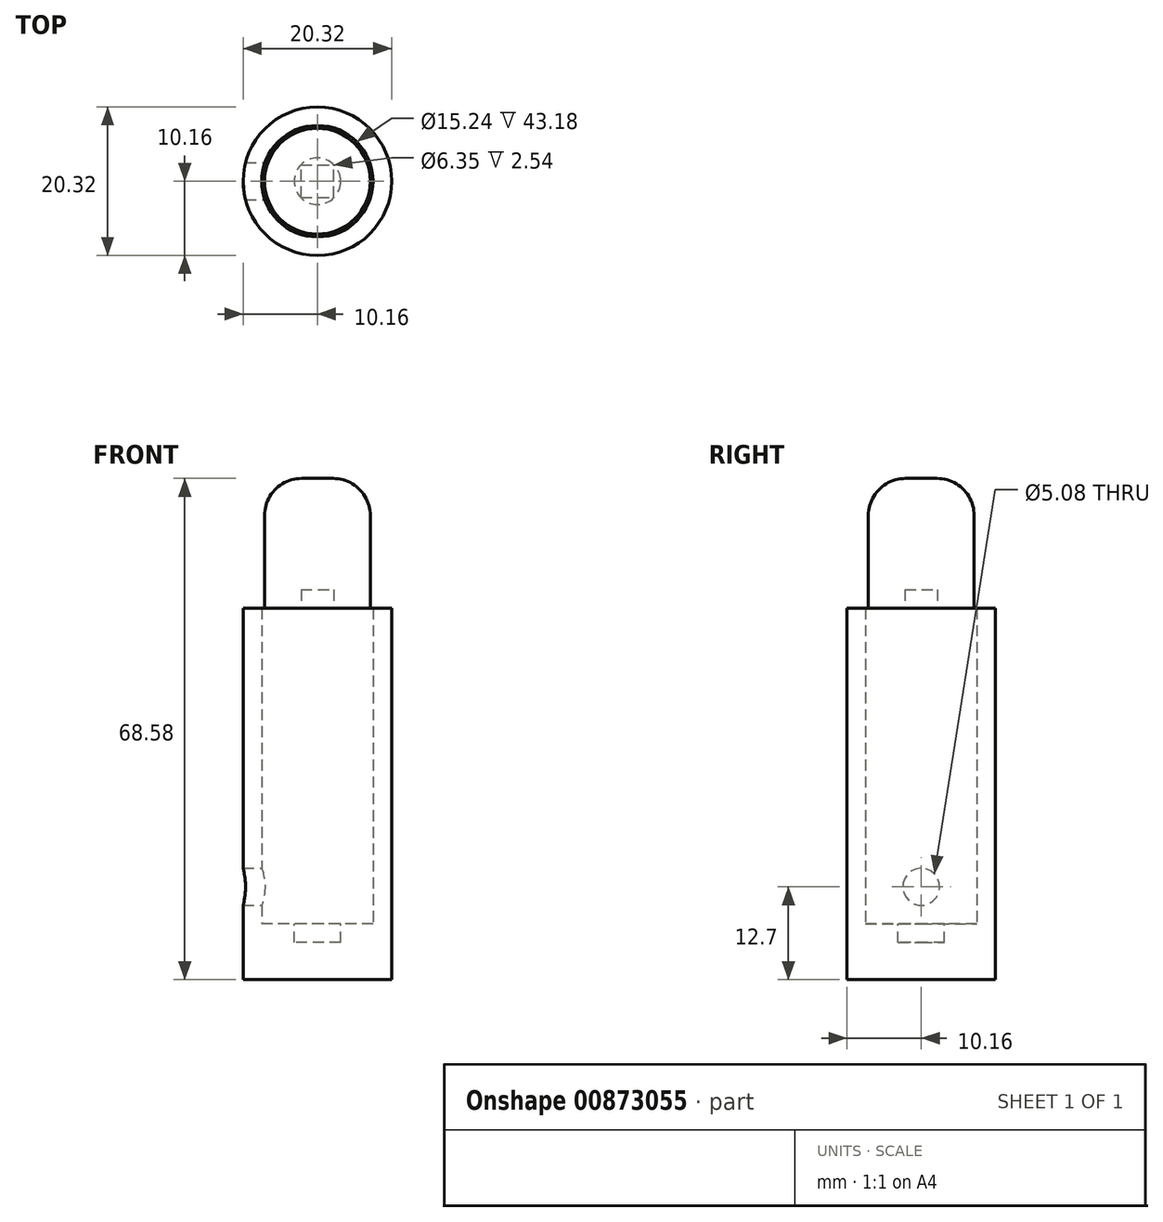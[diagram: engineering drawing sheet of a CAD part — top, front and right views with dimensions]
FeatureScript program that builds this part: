
annotation { "Feature Type Name" : "Feature", "Feature Type Description" : "" }
export const myFeature = defineFeature(function(context is Context, id is Id, definition is map)
    precondition{}
    {
        {
            var Q0;
            Q0=qCreatedBy(makeId("Top.planeOp"),FACE);
            var sketch = newSketch(context, id + "F0", { "sketchPlane" : qUnion([Q0])});
            skCircle(sketch, "E0", {"center": v(0, 0) * mm, "radius": 10.16 * mm});
            skSolve(sketch);
        }
        {
            var Q0;
            Q0=makeQuery(id+"F0.imprint","IMPRINT",FACE,{"disambiguationData":[TD([[makeQuery(id+"F0.imprint","IMPRINT",EDGE,{"derivedFrom":sQuery(id+"F0.wireOp",EDGE,"E0")}),1.0]])]});
            extrude(context, id + "F1", {"entities" : qUnion([Q0]), "depth" : 7.62 * mm, "offsetDistance" : 25.4 * mm});
        }
        {
            var Q0;
            Q0=makeQuery(id+"F1.opExtrude","CAP_FACE",FACE,{"disambiguationData":[OSD([sQuery(id+"F0.wireOp",EDGE,"E0")])],"isStart":false});
            var sketch = newSketch(context, id + "F2", { "sketchPlane" : qUnion([Q0])});
            skCircle(sketch, "E1", {"center": v(0, 0) * mm, "radius": 3.43 * mm});
            skCircle(sketch, "E2", {"center": v(0, 0) * mm, "radius": 7.62 * mm});
            skSolve(sketch);
        }
        {
            var Q0;
            Q0=makeQuery(id+"F2.imprint","IMPRINT",FACE,{"disambiguationData":[TD([[makeQuery(id+"F2.imprint","IMPRINT",EDGE,{"derivedFrom":sQuery(id+"F2.wireOp",EDGE,"E2")}),-1.0]])]});
            extrude(context, id + "F3", {"entities" : qUnion([Q0]), "operationType" : NewBodyOperationType.ADD, "depth" : 43.18 * mm, "offsetDistance" : 25.4 * mm});
        }
        {
            var Q0;
            Q0=makeQuery(id+"F1.opExtrude","CAP_FACE",FACE,{"disambiguationData":[OSD([sQuery(id+"F0.wireOp",EDGE,"E0")])],"isStart":false});
            var sketch = newSketch(context, id + "F4", { "sketchPlane" : qUnion([Q0])});
            skCircle(sketch, "E3", {"center": v(0, 0) * mm, "radius": 3.18 * mm});
            skSolve(sketch);
        }
        {
            var Q0;
            Q0 = qSketchRegion(id + "F4", true);
            extrude(context, id + "F5", {"entities" : qUnion([Q0]), "operationType" : NewBodyOperationType.REMOVE, "oppositeDirection" : true, "depth" : 2.54 * mm, "offsetDistance" : 25.4 * mm});
        }
        {
            var Q0;
            Q0=makeQuery(id+"F3.opExtrude","CAP_FACE",FACE,{"disambiguationData":[OSD([sQuery(id+"F0.wireOp",EDGE,"E0"),sQuery(id+"F2.wireOp",EDGE,"E2")])],"isStart":false});
            var sketch = newSketch(context, id + "F6", { "sketchPlane" : qUnion([Q0])});
            skCircle(sketch, "E4", {"center": v(0, 0) * mm, "radius": 7.24 * mm});
            skSolve(sketch);
        }
        {
            var Q0;
            Q0=makeQuery(id+"F6.imprint","IMPRINT",FACE,{"disambiguationData":[TD([[makeQuery(id+"F6.imprint","IMPRINT",EDGE,{"derivedFrom":sQuery(id+"F6.wireOp",EDGE,"E4")}),1.0]])]});
            extrude(context, id + "F7", {"entities" : qUnion([Q0]), "depth" : 17.78 * mm, "offsetDistance" : 25.4 * mm});
        }
        {
            var Q0;
            Q0=makeQuery(id+"F7.opExtrude","CAP_EDGE",EDGE,{"disambiguationData":[OSD([sQuery(id+"F6.wireOp",EDGE,"E4")])],"isStart":false});
            fillet(context, id + "F8", {"entities" : qUnion([Q0]), "radius" : 5.08 * mm, "tangentPropagation" : true, "allowEdgeOverflow" : false});
        }
        {
            var Q0;
            Q0=makeQuery(id+"F7.opExtrude","CAP_FACE",FACE,{"disambiguationData":[OSD([sQuery(id+"F6.wireOp",EDGE,"E4")])],"isStart":true});
            var sketch = newSketch(context, id + "F9", { "sketchPlane" : qUnion([Q0])});
            skLineSegment(sketch, "E5.bottom", {"start": v(-2.22, 2.22) * mm, "end": v(2.22, 2.22) * mm});
            skLineSegment(sketch, "E5.top", {"start": v(-2.22, -2.22) * mm, "end": v(2.22, -2.22) * mm});
            skLineSegment(sketch, "E5.left", {"start": v(-2.22, 2.22) * mm, "end": v(-2.22, -2.22) * mm});
            skLineSegment(sketch, "E5.right", {"start": v(2.22, 2.22) * mm, "end": v(2.22, -2.22) * mm});
            skSolve(sketch);
        }
        {
            var Q0;
            Q0=makeQuery(id+"F9.imprint","IMPRINT",FACE,{"disambiguationData":[TD([[makeQuery(id+"F9.imprint","IMPRINT",EDGE,{"derivedFrom":sQuery(id+"F9.wireOp",EDGE,"E5.bottom")}),-1.0]])]});
            extrude(context, id + "F10", {"entities" : qUnion([Q0]), "operationType" : NewBodyOperationType.REMOVE, "oppositeDirection" : true, "depth" : 2.54 * mm, "offsetDistance" : 25.4 * mm});
        }
        {
            var Q0;
            Q0=qCreatedBy(makeId("Right.planeOp"),FACE);
            var sketch = newSketch(context, id + "F11", { "sketchPlane" : qUnion([Q0])});
            skCircle(sketch, "E6", {"center": v(0, 12.7) * mm, "radius": 2.54 * mm});
            skSolve(sketch);
        }
        {
            var Q0;
            Q0 = qSketchRegion(id + "F11", true);
            extrude(context, id + "F12", {"entities" : qUnion([Q0]), "operationType" : NewBodyOperationType.REMOVE, "oppositeDirection" : true, "depth" : 25.4 * mm, "offsetDistance" : 25.4 * mm});
        }
    });
